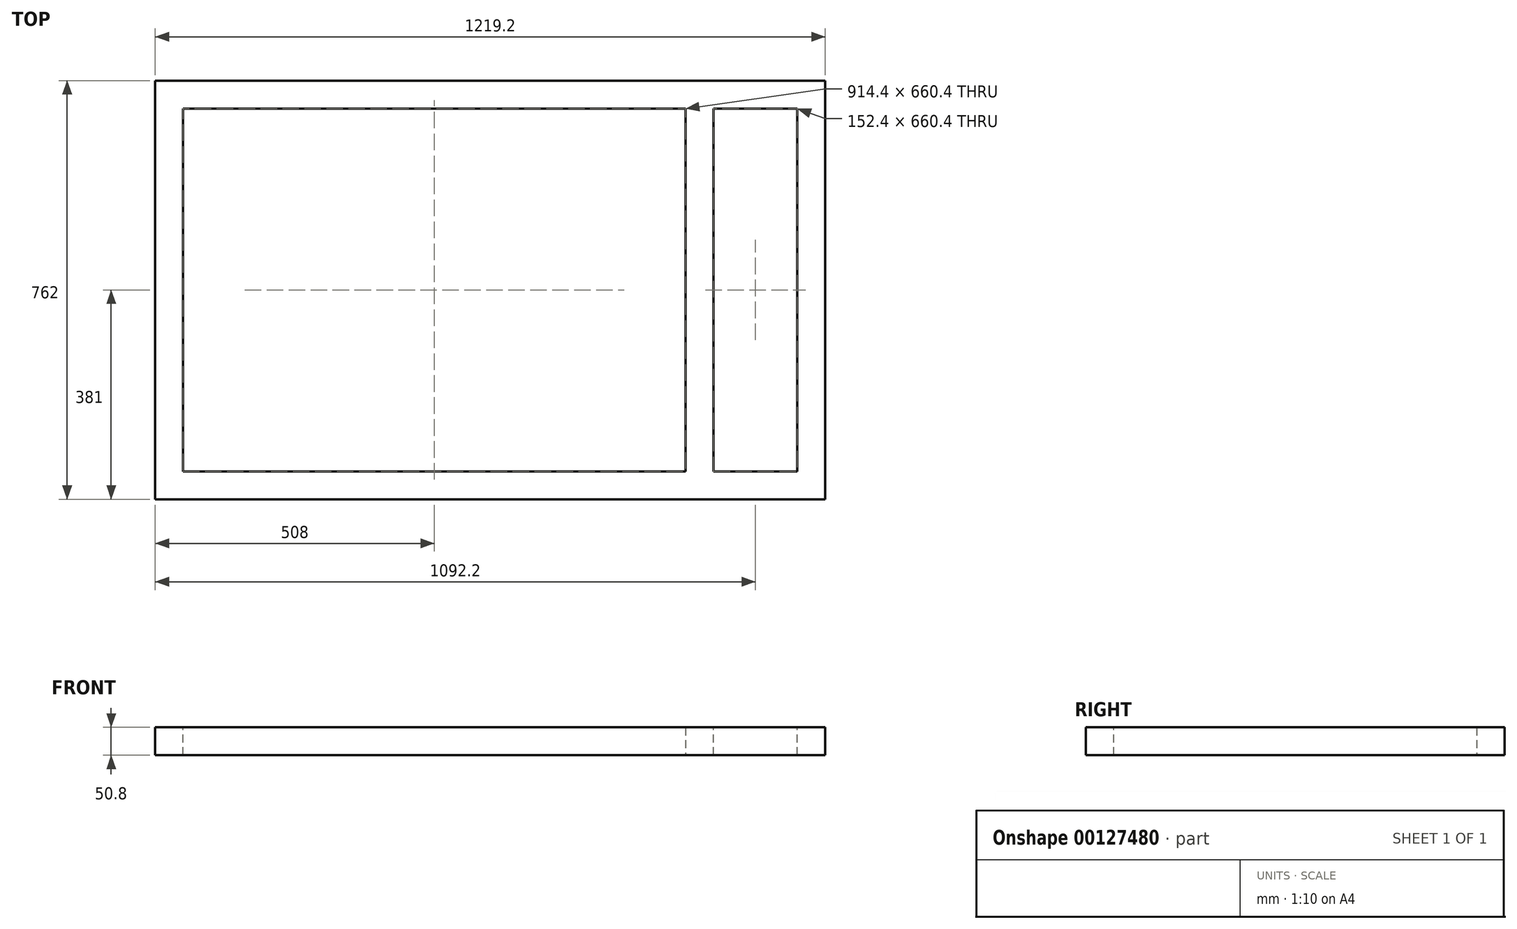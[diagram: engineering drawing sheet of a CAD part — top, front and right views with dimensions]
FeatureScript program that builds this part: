
annotation { "Feature Type Name" : "Feature", "Feature Type Description" : "" }
export const myFeature = defineFeature(function(context is Context, id is Id, definition is map)
    precondition{}
    {
        {
            var Q0;
            Q0=qCreatedBy(makeId("Top.planeOp"),FACE);
            var sketch = newSketch(context, id + "F0", { "sketchPlane" : qUnion([Q0])});
            skLineSegment(sketch, "E0.bottom", {"start": v(0, 0) * mm, "end": v(1219.2, 0) * mm});
            skLineSegment(sketch, "E0.top", {"start": v(0, 762) * mm, "end": v(1219.2, 762) * mm});
            skLineSegment(sketch, "E0.left", {"start": v(0, 0) * mm, "end": v(0, 762) * mm});
            skLineSegment(sketch, "E0.right", {"start": v(1219.2, 0) * mm, "end": v(1219.2, 762) * mm});
            skSolve(sketch);
        }
        {
            var Q0;
            Q0=qCreatedBy(makeId("Front.planeOp"),FACE);
            var sketch = newSketch(context, id + "F1", { "sketchPlane" : qUnion([Q0])});
            skLineSegment(sketch, "E1.bottom", {"start": v(0, 0) * mm, "end": v(50.8, 0) * mm});
            skLineSegment(sketch, "E1.top", {"start": v(0, -50.8) * mm, "end": v(50.8, -50.8) * mm});
            skLineSegment(sketch, "E1.left", {"start": v(0, 0) * mm, "end": v(0, -50.8) * mm});
            skLineSegment(sketch, "E1.right", {"start": v(50.8, 0) * mm, "end": v(50.8, -50.8) * mm});
            skSolve(sketch);
        }
        {
            var Q0;
            Q0 = qSketchRegion(id + "F1", true);
            var Q1;
            Q1=sQuery(id+"F0.wireOp",EDGE,"E0.left");
            var Q2;
            Q2=sQuery(id+"F0.wireOp",EDGE,"E0.top");
            var Q3;
            Q3=sQuery(id+"F0.wireOp",EDGE,"E0.right");
            var Q4;
            Q4=sQuery(id+"F0.wireOp",EDGE,"E0.bottom");
            sweep(context, id + "F2", {"profiles" : qUnion([Q0]), "path" : qUnion([Q1, Q2, Q3, Q4])});
        }
        {
            var Q0;
            Q0=makeQuery(id+"F2.opSweep","SWEPT_FACE",FACE,{"disambiguationData":[OSD([sQuery(id+"F0.wireOp",EDGE,"E0.top"),sQuery(id+"F1.wireOp",EDGE,"E1.right")])]});
            var sketch = newSketch(context, id + "F3", { "sketchPlane" : qUnion([Q0])});
            skLineSegment(sketch, "E2", {"start": v(1168.4, 0) * mm, "end": v(1016, 0) * mm, "construction": true});
            skLineSegment(sketch, "E3.bottom", {"start": v(1016, 0) * mm, "end": v(965.2, 0) * mm});
            skLineSegment(sketch, "E3.top", {"start": v(1016, -50.8) * mm, "end": v(965.2, -50.8) * mm});
            skLineSegment(sketch, "E3.left", {"start": v(1016, 0) * mm, "end": v(1016, -50.8) * mm});
            skLineSegment(sketch, "E3.right", {"start": v(965.2, 0) * mm, "end": v(965.2, -50.8) * mm});
            skSolve(sketch);
        }
        {
            var Q0;
            Q0=makeQuery(id+"F3.imprint","IMPRINT",FACE,{"disambiguationData":[TD([[makeQuery(id+"F3.imprint","IMPRINT",EDGE,{"derivedFrom":sQuery(id+"F3.wireOp",EDGE,"E3.bottom")}),-1.0]])]});
            var Q1;
            Q1=makeQuery(id+"F2.opSweep","SWEPT_FACE",FACE,{"disambiguationData":[OSD([sQuery(id+"F0.wireOp",EDGE,"E0.bottom"),sQuery(id+"F1.wireOp",EDGE,"E1.right")])]});
            extrude(context, id + "F4", {"entities" : qUnion([Q0]), "operationType" : NewBodyOperationType.ADD, "endBound" : BoundingType.UP_TO_SURFACE, "endBoundEntityFace" : qUnion([Q1]), "depth" : 25.4 * mm});
        }
    });
